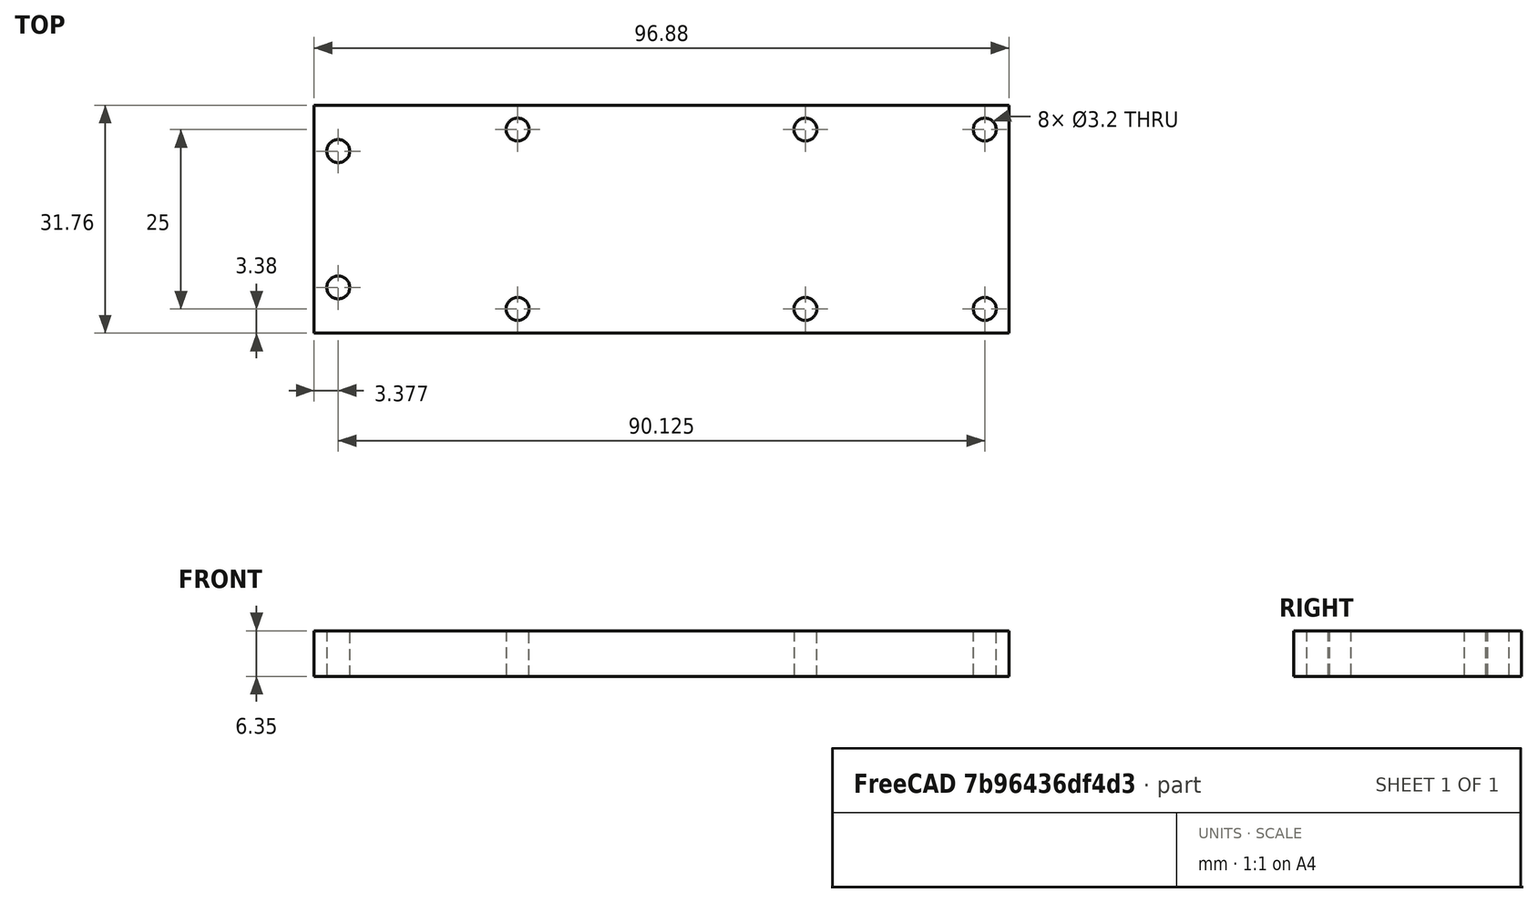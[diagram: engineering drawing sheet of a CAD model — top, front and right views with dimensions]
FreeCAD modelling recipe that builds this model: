
FCSTD DOCUMENT  (FreeCAD 0.21R33771 (Git))
Label: Connector Plate
License: All rights reserved
LicenseURL: http://en.wikipedia.org/wiki/All_rights_reserved
objects: PartDesign::CoordinateSystem×2, Sketcher::SketchObject×1, PartDesign::Pad×1, PartDesign::Body×1
note: 6 computed .brp shape members not serialized (recipe doc carries the construction recipe); baked Part::Feature solids carry a one-line shape summary decoded from their .brp

FEATURE [Sketcher::SketchObject] Sketch
  FullyConstrained = true
  MapMode = 5
  Support = -> [XY_Plane]
  expr: Constraints[59] = 63 + 18
  sketch-geometry (28):
    g0: LineSegment StartX=-20.0625 StartY=12.5 StartZ=0 EndX=-20.0625 EndY=-12.5 EndZ=0
    g1: LineSegment StartX=-20.0625 StartY=-12.5 StartZ=0 EndX=20.0625 EndY=-12.5 EndZ=0
    g2: LineSegment StartX=20.0625 StartY=-12.5 StartZ=0 EndX=20.0625 EndY=12.5 EndZ=0
    g3: LineSegment StartX=20.0625 StartY=12.5 StartZ=0 EndX=-20.0625 EndY=12.5 EndZ=0
    g4: LineSegment StartX=-45.0625 StartY=12.5 StartZ=0 EndX=-45.0625 EndY=-12.5 EndZ=0
    g5: LineSegment StartX=45.0625 StartY=-12.5 StartZ=0 EndX=45.0625 EndY=12.5 EndZ=0
    g6: LineSegment StartX=45.0625 StartY=12.5 StartZ=0 EndX=20.0625 EndY=12.5 EndZ=0
    g7: LineSegment StartX=20.0625 StartY=-12.5 StartZ=0 EndX=45.0625 EndY=-12.5 EndZ=0
    g8: LineSegment StartX=-45.0625 StartY=-12.5 StartZ=0 EndX=-20.0625 EndY=-12.5 EndZ=0
    g9: LineSegment StartX=-20.0625 StartY=-12.5 StartZ=0 EndX=20.0625 EndY=-12.5 EndZ=0
    g10: LineSegment StartX=20.0625 StartY=12.5 StartZ=0 EndX=-20.0625 EndY=12.5 EndZ=0
    g11: LineSegment StartX=-20.0625 StartY=12.5 StartZ=0 EndX=-45.0625 EndY=12.5 EndZ=0
    g12: Circle CenterX=-45.0625 CenterY=9.5 CenterZ=0 NormalX=0 NormalY=0 NormalZ=1 AngleXU=0 Radius=1.6
    g13: Circle CenterX=-20.0625 CenterY=12.5 CenterZ=0 NormalX=0 NormalY=0 NormalZ=1 AngleXU=0 Radius=1.6
    g14: Circle CenterX=20.0625 CenterY=12.5 CenterZ=0 NormalX=0 NormalY=0 NormalZ=1 AngleXU=0 Radius=1.6
    g15: Circle CenterX=45.0625 CenterY=12.5 CenterZ=0 NormalX=0 NormalY=0 NormalZ=1 AngleXU=0 Radius=1.6
    g16: Circle CenterX=45.0625 CenterY=-12.5 CenterZ=0 NormalX=0 NormalY=0 NormalZ=1 AngleXU=0 Radius=1.6
    g17: Circle CenterX=20.0625 CenterY=-12.5 CenterZ=0 NormalX=0 NormalY=0 NormalZ=1 AngleXU=0 Radius=1.6
    g18: Circle CenterX=-20.0625 CenterY=-12.5 CenterZ=0 NormalX=0 NormalY=0 NormalZ=1 AngleXU=0 Radius=1.6
    g19: Circle CenterX=-45.0625 CenterY=-9.5 CenterZ=0 NormalX=0 NormalY=0 NormalZ=1 AngleXU=0 Radius=1.6
    g20: LineSegment StartX=-48.4375 StartY=15.875 StartZ=0 EndX=-48.4375 EndY=-15.875 EndZ=0
    g21: LineSegment StartX=-48.4375 StartY=-15.875 StartZ=0 EndX=48.4375 EndY=-15.875 EndZ=0
    g22: LineSegment StartX=48.4375 StartY=-15.875 StartZ=0 EndX=48.4375 EndY=15.875 EndZ=0
    g23: LineSegment StartX=48.4375 StartY=15.875 StartZ=0 EndX=-48.4375 EndY=15.875 EndZ=0
    g24: LineSegment StartX=-48.4375 StartY=12.5 StartZ=0 EndX=-45.0625 EndY=12.5 EndZ=0
    g25: LineSegment StartX=-45.0625 StartY=12.5 StartZ=0 EndX=-45.0625 EndY=15.875 EndZ=0
    g26: LineSegment StartX=20.0625 StartY=12.5 StartZ=0 EndX=45.0625 EndY=-12.5 EndZ=0
    g27: GeomPoint X=32.5625 Y=0 Z=0
  constraints (65):
    c: Coincident(g0,g1)
    c: Coincident(g1,g2)
    c: Coincident(g2,g3)
    c: Coincident(g3,g0)
    c: Horizontal(g1)
    c: Horizontal(g3)
    c: Vertical(g0)
    c: Vertical(g2)
    c: Coincident(g4,g8)
    c: Coincident(g7,g5)
    c: Coincident(g5,g6)
    c: Coincident(g11,g4)
    c: Vertical(g4)
    c: Vertical(g5)
    c: Coincident(g6,g10)
    c: Horizontal(g6)
    c: Coincident(g9,g7)
    c: Horizontal(g7)
    c: Coincident(g8,g9)
    c: Horizontal(g8)
    c: Coincident(g10,g11)
    c: Coincident(g6,g2)
    c: Coincident(g7,g1)
    c: Coincident(g8,g0)
    c: Coincident(g10,g0)
    c: Equal(g6,g5)
    c: DistanceY(g5,g5) = 25
    c: Coincident(g13,g0)
    c: Coincident(g14,g2)
    c: Coincident(g15,g5)
    c: Coincident(g16,g5)
    c: Coincident(g17,g1)
    c: Coincident(g18,g0)
    c: Equal(g12,g13)
    c: Equal(g12,g18)
    c: Equal(g12,g19)
    c: Equal(g12, g14-g17) x4
    c: Diameter(g12) = 3.2
    c: Coincident(g20,g21)
    c: Coincident(g21,g22)
    c: Coincident(g22,g23)
    c: Coincident(g23,g20)
    c: Horizontal(g21)
    c: Horizontal(g23)
    c: Vertical(g20)
    c: Vertical(g22)
    c: DistanceY(g22,g22) = 31.75
    c: PointOnObject(g24,g20)
    c: Horizontal(g24)
    c: PointOnObject(g25,g23)
    c: Vertical(g25)
    c: Equal(g24,g25)
    c: Coincident(g26,g14)
    c: Coincident(g26,g16)
    c: PointOnObject(g27,g26)
    c: PointOnObject(g27,g-1)
    c: DistanceX(g20,g27) = 81
    c: Coincident(g25,g24)
    c: Coincident(g25,g4)
    c: PointOnObject(g19,g4)
    c: Symmetric(g12,g19,g-1)
    c: DistanceY(g19,g12) = 19
    c: Symmetric(g16,g4,g-1)
    c: Symmetric(g17,g13,g-1)
    c: Symmetric(g21,g20,g-1)
FEATURE [PartDesign::Pad] Pad
  Direction = (0,0,1)
  Length = 6.35
  Length2 = 10
  Profile = -> Sketch
  ReferenceAxis = -> Sketch [N_Axis]
  Type = 0
FEATURE [PartDesign::CoordinateSystem] Local_CS
  AttacherType = Attacher::AttachEngine3D
  MapMode = 45
  Placement = pos=(-32.5625,0,3.175) rot=(0,0,1;1.5708rad)
  Support = -> [Pad]
FEATURE [PartDesign::CoordinateSystem] Local_CS001
  AttacherType = Attacher::AttachEngine3D
  AttachmentOffset = pos=(0,0,0) rot=(1,0,0;0.785398rad)
  MapMode = 45
  Placement = pos=(32.5625,0,3.175) rot=(0.57735,0.57735,0.57735;4.18879rad)
  Support = -> [Pad]
FEATURE [PartDesign::Body] Body  label="Connector Plate"
  Group = -> [Sketch,Pad,Local_CS,Local_CS001]
  Origin = -> Origin
  Tip = -> Pad
